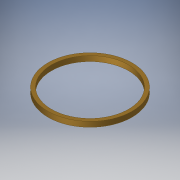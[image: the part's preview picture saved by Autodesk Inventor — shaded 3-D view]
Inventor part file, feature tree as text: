
AUTODESK INVENTOR PART (.ipt)
format: ipt  version: 2018 (Build 220112000, 112)  size: 101,888 bytes
history: native  units: in
note: dims shown in document units (in); Inventor stores cm internally (conversion verified against a paired STEP export)
features: extrude x1, sketch x1
ambient origin geometry x8: Origin, YZ Plane, XZ Plane, XY Plane, X Axis, Y Axis, Z Axis, Center Point
bodies: Solid1 (feature_tree)
feature tree (2):
  extrude  "Extrusion1"  Depth=0.5in
  sketch  "Sketch1"  dims[d0=8.18in d1=7.5in d2=0.5in d3=0.0in]
